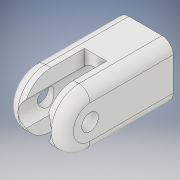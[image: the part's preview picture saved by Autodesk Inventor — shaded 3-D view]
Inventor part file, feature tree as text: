
AUTODESK INVENTOR PART (.ipt)
format: ipt  version: 2017 SP1 (Build 210196100, 196)  size: 199,168 bytes
history: native  units: in
note: dims shown in document units (in); Inventor stores cm internally (conversion verified against a paired STEP export)
features: extrude x6, sketch x6, fillet x1, plane x1, projected_geometry x1
ambient origin geometry x8: Origin, YZ Plane, XZ Plane, XY Plane, X Axis, Y Axis, Z Axis, Center Point
bodies: Solid1 (feature_tree)
feature tree (15):
  extrude  "Extrusion1"  Depth=0.3937in
  extrude  "Extrusion2"  Depth=0.3937in
  extrude  "Extrusion3"  Depth=0.1181in
  fillet  "Fillet1"  Radius=0.1181in
  extrude  "Extrusion4"  Depth=0.1181in
  plane  "Work Plane1"
  extrude  "Extrusion5"  Depth=0.1181in TaperAngle=0.0deg
  extrude  "Extrusion6"  Depth=0.0394in
  sketch  "Sketch1"  dims[d0=0.3937in d1=0.3937in]
  sketch  "Sketch2"  dims[d2=0.3543in d3=0.0in d4=0.3937in]
  sketch  "Sketch3"  dims[d5=0.5906in d6=0.1181in d7=0.1181in d8=0.0in]
  projected_geometry  "Projected Loop1"
  sketch  "Sketch4"  dims[d9=0.1181in d10=0.0in d11=0.0787in]
  sketch  "Sketch5"  dims[d12=0.1575in d13=0.1181in d14=0.0in]
  sketch  "Sketch8"  dims[d15=-0.1181in d16=0.2362in d17=0.1181in d18=0.0in d20=0.2362in d21=0.0394in d22=0.0in]
